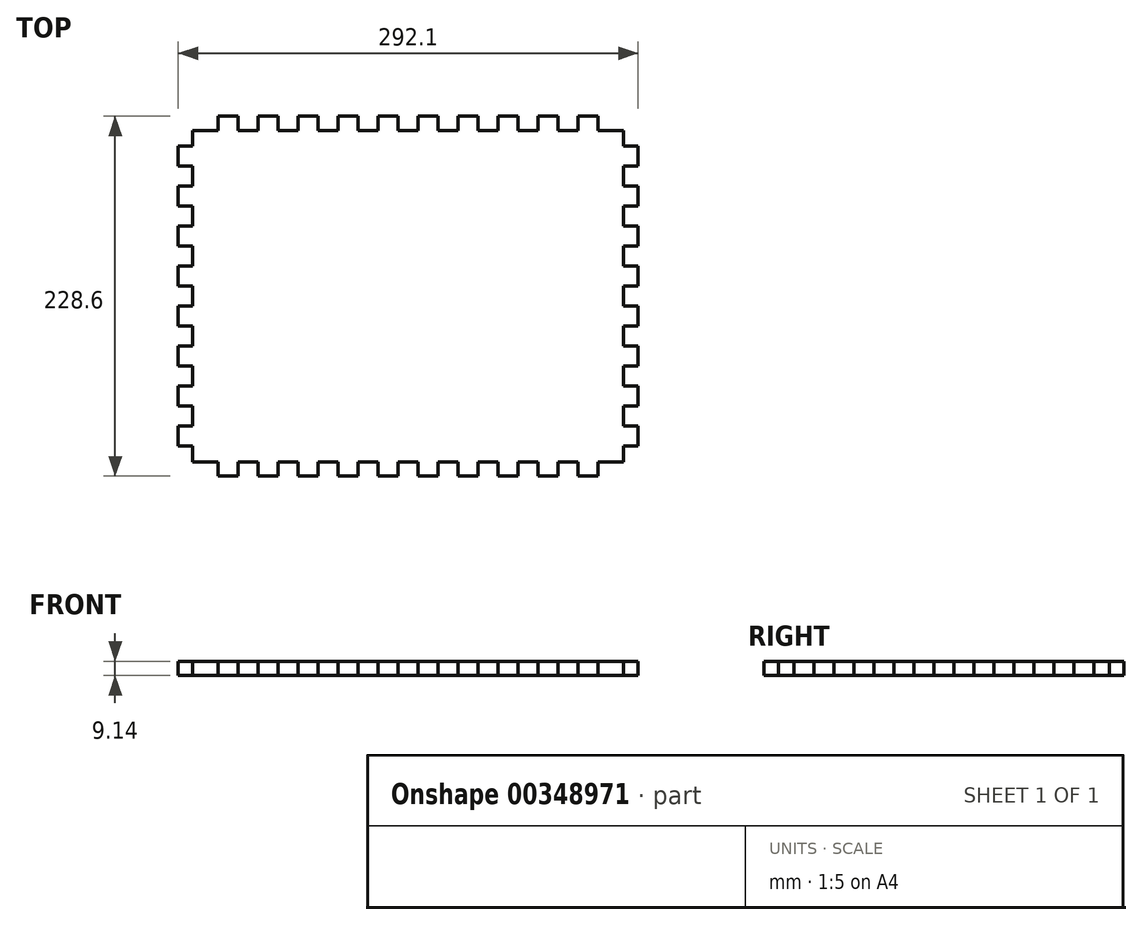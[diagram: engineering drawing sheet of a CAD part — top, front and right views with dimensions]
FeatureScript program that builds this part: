
annotation { "Feature Type Name" : "Feature", "Feature Type Description" : "" }
export const myFeature = defineFeature(function(context is Context, id is Id, definition is map)
    precondition{}
    {
        {
            var Q0;
            Q0=qCreatedBy(makeId("Top.planeOp"),FACE);
            var sketch = newSketch(context, id + "F0", { "sketchPlane" : qUnion([Q0])});
            skLineSegment(sketch, "E0.bottom", {"start": v(0, 0) * mm, "end": v(25.4, 0) * mm, "construction": true});
            skLineSegment(sketch, "E1.bottom", {"start": v(9.14, -9.14) * mm, "end": v(25.4, -9.14) * mm});
            skLineSegment(sketch, "E1.left", {"start": v(9.14, -9.14) * mm, "end": v(9.14, -19.05) * mm});
            skLineSegment(sketch, "E2", {"start": v(9.14, -19.05) * mm, "end": v(0, -19.05) * mm});
            skLineSegment(sketch, "E3", {"start": v(25.4, -9.14) * mm, "end": v(25.4, 0) * mm});
            skLineSegment(sketch, "E4", {"start": v(38.1, 0) * mm, "end": v(38.1, -9.14) * mm});
            skLineSegment(sketch, "E5.0", {"start": v(50.8, 0) * mm, "end": v(50.8, -9.14) * mm});
            skLineSegment(sketch, "E6.0", {"start": v(63.5, 0) * mm, "end": v(63.5, -9.14) * mm});
            skLineSegment(sketch, "E7.0", {"start": v(76.2, 0) * mm, "end": v(76.2, -9.14) * mm});
            skLineSegment(sketch, "E8.0", {"start": v(88.9, 0) * mm, "end": v(88.9, -9.14) * mm});
            skLineSegment(sketch, "E9.0", {"start": v(101.6, 0) * mm, "end": v(101.6, -9.14) * mm});
            skLineSegment(sketch, "E10.0", {"start": v(114.3, 0) * mm, "end": v(114.3, -9.14) * mm});
            skLineSegment(sketch, "E11.0", {"start": v(127, 0) * mm, "end": v(127, -9.14) * mm});
            skLineSegment(sketch, "E12.0", {"start": v(139.7, 0) * mm, "end": v(139.7, -9.14) * mm});
            skLineSegment(sketch, "E13.trimOffspring", {"start": v(50.8, 0) * mm, "end": v(63.5, 0) * mm});
            skLineSegment(sketch, "E14.trimOffspring", {"start": v(63.5, -9.14) * mm, "end": v(76.2, -9.14) * mm});
            skLineSegment(sketch, "E15.trimOffspring", {"start": v(76.2, 0) * mm, "end": v(88.9, 0) * mm});
            skLineSegment(sketch, "E16.trimOffspring", {"start": v(88.9, -9.14) * mm, "end": v(101.6, -9.14) * mm});
            skLineSegment(sketch, "E17.trimOffspring", {"start": v(101.6, 0) * mm, "end": v(114.3, 0) * mm});
            skLineSegment(sketch, "E18.trimOffspring", {"start": v(114.3, -9.14) * mm, "end": v(127, -9.14) * mm});
            skLineSegment(sketch, "E19.trimOffspring", {"start": v(127, 0) * mm, "end": v(139.7, 0) * mm});
            skLineSegment(sketch, "E20.trimOffspring", {"start": v(139.7, -9.14) * mm, "end": v(146.05, -9.14) * mm});
            skLineSegment(sketch, "E21.trimOffspring", {"start": v(38.1, -9.14) * mm, "end": v(50.8, -9.14) * mm});
            skLineSegment(sketch, "E22", {"start": v(0, -31.75) * mm, "end": v(9.14, -31.75) * mm});
            skLineSegment(sketch, "E23", {"start": v(9.14, -31.75) * mm, "end": v(9.14, -44.45) * mm});
            skLineSegment(sketch, "E24", {"start": v(9.14, -44.45) * mm, "end": v(0, -44.45) * mm});
            skLineSegment(sketch, "E25.0", {"start": v(9.14, -57.15) * mm, "end": v(0, -57.15) * mm});
            skLineSegment(sketch, "E26.0", {"start": v(9.14, -69.85) * mm, "end": v(0, -69.85) * mm});
            skLineSegment(sketch, "E27.0", {"start": v(9.14, -82.55) * mm, "end": v(0, -82.55) * mm});
            skLineSegment(sketch, "E28.0", {"start": v(9.14, -95.25) * mm, "end": v(0, -95.25) * mm});
            skLineSegment(sketch, "E29.0", {"start": v(9.14, -107.95) * mm, "end": v(0, -107.95) * mm});
            skLineSegment(sketch, "E30.trimOffspring", {"start": v(0, -44.45) * mm, "end": v(0, -57.15) * mm});
            skLineSegment(sketch, "E31.trimOffspring", {"start": v(9.14, -57.15) * mm, "end": v(9.14, -69.85) * mm});
            skLineSegment(sketch, "E32.trimOffspring", {"start": v(0, -69.85) * mm, "end": v(0, -82.55) * mm});
            skLineSegment(sketch, "E33.trimOffspring", {"start": v(9.14, -82.55) * mm, "end": v(9.14, -95.25) * mm});
            skLineSegment(sketch, "E34.trimOffspring", {"start": v(0, -95.25) * mm, "end": v(0, -107.95) * mm});
            skLineSegment(sketch, "E35.trimOffspring", {"start": v(9.14, -107.95) * mm, "end": v(9.14, -114.3) * mm});
            skLineSegment(sketch, "E36", {"start": v(0, 0) * mm, "end": v(0, -19.05) * mm, "construction": true});
            skLineSegment(sketch, "E37", {"start": v(0, -19.05) * mm, "end": v(0, -31.75) * mm});
            skLineSegment(sketch, "E38", {"start": v(25.4, 0) * mm, "end": v(38.1, 0) * mm});
            skLineSegment(sketch, "E39", {"start": v(146.05, -9.14) * mm, "end": v(146.05, -114.3) * mm, "construction": true});
            skLineSegment(sketch, "E40", {"start": v(9.14, -114.3) * mm, "end": v(146.05, -114.3) * mm, "construction": true});
            skLineSegment(sketch, "E41.MirrorCS", {"start": v(9.14, -120.65) * mm, "end": v(9.14, -114.3) * mm});
            skLineSegment(sketch, "E42.MirrorCS", {"start": v(9.14, -120.65) * mm, "end": v(0, -120.65) * mm});
            skLineSegment(sketch, "E43.MirrorCS", {"start": v(0, -133.35) * mm, "end": v(0, -120.65) * mm});
            skLineSegment(sketch, "E44.MirrorCS", {"start": v(9.14, -133.35) * mm, "end": v(0, -133.35) * mm});
            skLineSegment(sketch, "E45.MirrorCS", {"start": v(9.14, -146.05) * mm, "end": v(9.14, -133.35) * mm});
            skLineSegment(sketch, "E46.MirrorCS", {"start": v(9.14, -146.05) * mm, "end": v(0, -146.05) * mm});
            skLineSegment(sketch, "E47.MirrorCS", {"start": v(0, -158.75) * mm, "end": v(0, -146.05) * mm});
            skLineSegment(sketch, "E48.MirrorCS", {"start": v(9.14, -158.75) * mm, "end": v(0, -158.75) * mm});
            skLineSegment(sketch, "E49.MirrorCS", {"start": v(9.14, -171.45) * mm, "end": v(9.14, -158.75) * mm});
            skLineSegment(sketch, "E50.MirrorCS", {"start": v(9.14, -171.45) * mm, "end": v(0, -171.45) * mm});
            skLineSegment(sketch, "E51.MirrorCS", {"start": v(0, -184.15) * mm, "end": v(0, -171.45) * mm});
            skLineSegment(sketch, "E52.MirrorCS", {"start": v(9.14, -184.15) * mm, "end": v(0, -184.15) * mm});
            skLineSegment(sketch, "E53.MirrorCS", {"start": v(9.14, -196.85) * mm, "end": v(9.14, -184.15) * mm});
            skLineSegment(sketch, "E54.MirrorCS", {"start": v(0, -196.85) * mm, "end": v(9.14, -196.85) * mm});
            skLineSegment(sketch, "E55.MirrorCS", {"start": v(0, -209.55) * mm, "end": v(0, -196.85) * mm});
            skLineSegment(sketch, "E56.MirrorCS", {"start": v(9.14, -209.55) * mm, "end": v(0, -209.55) * mm});
            skLineSegment(sketch, "E57.MirrorCS", {"start": v(9.14, -219.46) * mm, "end": v(9.14, -209.55) * mm});
            skLineSegment(sketch, "E58.MirrorCS", {"start": v(9.14, -219.46) * mm, "end": v(25.4, -219.46) * mm});
            skLineSegment(sketch, "E59.MirrorCS", {"start": v(25.4, -219.46) * mm, "end": v(25.4, -228.6) * mm});
            skLineSegment(sketch, "E60.MirrorCS", {"start": v(25.4, -228.6) * mm, "end": v(38.1, -228.6) * mm});
            skLineSegment(sketch, "E61.MirrorCS", {"start": v(38.1, -228.6) * mm, "end": v(38.1, -219.46) * mm});
            skLineSegment(sketch, "E62.MirrorCS", {"start": v(38.1, -219.46) * mm, "end": v(50.8, -219.46) * mm});
            skLineSegment(sketch, "E63.MirrorCS", {"start": v(50.8, -228.6) * mm, "end": v(50.8, -219.46) * mm});
            skLineSegment(sketch, "E64.MirrorCS", {"start": v(50.8, -228.6) * mm, "end": v(63.5, -228.6) * mm});
            skLineSegment(sketch, "E65.MirrorCS", {"start": v(63.5, -228.6) * mm, "end": v(63.5, -219.46) * mm});
            skLineSegment(sketch, "E66.MirrorCS", {"start": v(63.5, -219.46) * mm, "end": v(76.2, -219.46) * mm});
            skLineSegment(sketch, "E67.MirrorCS", {"start": v(76.2, -228.6) * mm, "end": v(76.2, -219.46) * mm});
            skLineSegment(sketch, "E68.MirrorCS", {"start": v(76.2, -228.6) * mm, "end": v(88.9, -228.6) * mm});
            skLineSegment(sketch, "E69.MirrorCS", {"start": v(88.9, -228.6) * mm, "end": v(88.9, -219.46) * mm});
            skLineSegment(sketch, "E70.MirrorCS", {"start": v(88.9, -219.46) * mm, "end": v(101.6, -219.46) * mm});
            skLineSegment(sketch, "E71.MirrorCS", {"start": v(101.6, -228.6) * mm, "end": v(101.6, -219.46) * mm});
            skLineSegment(sketch, "E72.MirrorCS", {"start": v(101.6, -228.6) * mm, "end": v(114.3, -228.6) * mm});
            skLineSegment(sketch, "E73.MirrorCS", {"start": v(114.3, -219.46) * mm, "end": v(127, -219.46) * mm});
            skLineSegment(sketch, "E74.MirrorCS", {"start": v(127, -228.6) * mm, "end": v(127, -219.46) * mm});
            skLineSegment(sketch, "E75.MirrorCS", {"start": v(127, -228.6) * mm, "end": v(139.7, -228.6) * mm});
            skLineSegment(sketch, "E76.MirrorCS", {"start": v(139.7, -228.6) * mm, "end": v(139.7, -219.46) * mm});
            skLineSegment(sketch, "E77.MirrorCS", {"start": v(139.7, -219.46) * mm, "end": v(146.05, -219.46) * mm});
            skLineSegment(sketch, "E78.MirrorCS", {"start": v(114.3, -228.6) * mm, "end": v(114.3, -219.46) * mm});
            skLineSegment(sketch, "E79.MirrorCS", {"start": v(152.4, -9.14) * mm, "end": v(146.05, -9.14) * mm});
            skLineSegment(sketch, "E80.MirrorCS", {"start": v(152.4, 0) * mm, "end": v(152.4, -9.14) * mm});
            skLineSegment(sketch, "E81.MirrorCS", {"start": v(165.1, 0) * mm, "end": v(152.4, 0) * mm});
            skLineSegment(sketch, "E82.MirrorCS", {"start": v(165.1, 0) * mm, "end": v(165.1, -9.14) * mm});
            skLineSegment(sketch, "E83.MirrorCS", {"start": v(177.8, -9.14) * mm, "end": v(165.1, -9.14) * mm});
            skLineSegment(sketch, "E84.MirrorCS", {"start": v(177.8, 0) * mm, "end": v(177.8, -9.14) * mm});
            skLineSegment(sketch, "E85.MirrorCS", {"start": v(190.5, 0) * mm, "end": v(177.8, 0) * mm});
            skLineSegment(sketch, "E86.MirrorCS", {"start": v(190.5, 0) * mm, "end": v(190.5, -9.14) * mm});
            skLineSegment(sketch, "E87.MirrorCS", {"start": v(203.2, -9.14) * mm, "end": v(190.5, -9.14) * mm});
            skLineSegment(sketch, "E88.MirrorCS", {"start": v(203.2, 0) * mm, "end": v(203.2, -9.14) * mm});
            skLineSegment(sketch, "E89.MirrorCS", {"start": v(215.9, 0) * mm, "end": v(203.2, 0) * mm});
            skLineSegment(sketch, "E90.MirrorCS", {"start": v(215.9, 0) * mm, "end": v(215.9, -9.14) * mm});
            skLineSegment(sketch, "E91.MirrorCS", {"start": v(228.6, -9.14) * mm, "end": v(215.9, -9.14) * mm});
            skLineSegment(sketch, "E92.MirrorCS", {"start": v(228.6, 0) * mm, "end": v(228.6, -9.14) * mm});
            skLineSegment(sketch, "E93.MirrorCS", {"start": v(241.3, 0) * mm, "end": v(228.6, 0) * mm});
            skLineSegment(sketch, "E94.MirrorCS", {"start": v(241.3, 0) * mm, "end": v(241.3, -9.14) * mm});
            skLineSegment(sketch, "E95.MirrorCS", {"start": v(254, -9.14) * mm, "end": v(241.3, -9.14) * mm});
            skLineSegment(sketch, "E96.MirrorCS", {"start": v(254, 0) * mm, "end": v(254, -9.14) * mm});
            skLineSegment(sketch, "E97.MirrorCS", {"start": v(266.7, 0) * mm, "end": v(254, 0) * mm});
            skLineSegment(sketch, "E98.MirrorCS", {"start": v(266.7, -9.14) * mm, "end": v(266.7, 0) * mm});
            skLineSegment(sketch, "E99.MirrorCS", {"start": v(282.96, -9.14) * mm, "end": v(266.7, -9.14) * mm});
            skLineSegment(sketch, "E100.MirrorCS", {"start": v(282.96, -31.75) * mm, "end": v(282.96, -44.45) * mm});
            skLineSegment(sketch, "E101.MirrorCS", {"start": v(282.96, -107.95) * mm, "end": v(282.96, -114.3) * mm});
            skLineSegment(sketch, "E102.MirrorCS", {"start": v(282.96, -120.65) * mm, "end": v(282.96, -114.3) * mm});
            skLineSegment(sketch, "E103.MirrorCS", {"start": v(292.1, -95.25) * mm, "end": v(292.1, -107.95) * mm});
            skLineSegment(sketch, "E104.MirrorCS", {"start": v(282.96, -171.45) * mm, "end": v(282.96, -158.75) * mm});
            skLineSegment(sketch, "E105.MirrorCS", {"start": v(282.96, -209.55) * mm, "end": v(292.1, -209.55) * mm});
            skLineSegment(sketch, "E106.MirrorCS", {"start": v(282.96, -57.15) * mm, "end": v(292.1, -57.15) * mm});
            skLineSegment(sketch, "E107.MirrorCS", {"start": v(282.96, -196.85) * mm, "end": v(282.96, -184.15) * mm});
            skLineSegment(sketch, "E108.MirrorCS", {"start": v(292.1, -31.75) * mm, "end": v(282.96, -31.75) * mm});
            skLineSegment(sketch, "E109.MirrorCS", {"start": v(292.1, -44.45) * mm, "end": v(292.1, -57.15) * mm});
            skLineSegment(sketch, "E110.MirrorCS", {"start": v(282.96, -82.55) * mm, "end": v(292.1, -82.55) * mm});
            skLineSegment(sketch, "E111.MirrorCS", {"start": v(282.96, -44.45) * mm, "end": v(292.1, -44.45) * mm});
            skLineSegment(sketch, "E112.MirrorCS", {"start": v(292.1, -133.35) * mm, "end": v(292.1, -120.65) * mm});
            skLineSegment(sketch, "E113.MirrorCS", {"start": v(282.96, -146.05) * mm, "end": v(282.96, -133.35) * mm});
            skLineSegment(sketch, "E114.MirrorCS", {"start": v(282.96, -19.05) * mm, "end": v(292.1, -19.05) * mm});
            skLineSegment(sketch, "E115.MirrorCS", {"start": v(282.96, -95.25) * mm, "end": v(292.1, -95.25) * mm});
            skLineSegment(sketch, "E116.MirrorCS", {"start": v(292.1, -196.85) * mm, "end": v(282.96, -196.85) * mm});
            skLineSegment(sketch, "E117.MirrorCS", {"start": v(292.1, -158.75) * mm, "end": v(292.1, -146.05) * mm});
            skLineSegment(sketch, "E118.MirrorCS", {"start": v(282.96, -107.95) * mm, "end": v(292.1, -107.95) * mm});
            skLineSegment(sketch, "E119.MirrorCS", {"start": v(282.96, -69.85) * mm, "end": v(292.1, -69.85) * mm});
            skLineSegment(sketch, "E120.MirrorCS", {"start": v(292.1, -184.15) * mm, "end": v(292.1, -171.45) * mm});
            skLineSegment(sketch, "E121.MirrorCS", {"start": v(282.96, -184.15) * mm, "end": v(292.1, -184.15) * mm});
            skLineSegment(sketch, "E122.MirrorCS", {"start": v(292.1, -69.85) * mm, "end": v(292.1, -82.55) * mm});
            skLineSegment(sketch, "E123.MirrorCS", {"start": v(282.96, -158.75) * mm, "end": v(292.1, -158.75) * mm});
            skLineSegment(sketch, "E124.MirrorCS", {"start": v(282.96, -120.65) * mm, "end": v(292.1, -120.65) * mm});
            skLineSegment(sketch, "E125.MirrorCS", {"start": v(282.96, -146.05) * mm, "end": v(292.1, -146.05) * mm});
            skLineSegment(sketch, "E126.MirrorCS", {"start": v(292.1, -19.05) * mm, "end": v(292.1, -31.75) * mm});
            skLineSegment(sketch, "E127.MirrorCS", {"start": v(282.96, -171.45) * mm, "end": v(292.1, -171.45) * mm});
            skLineSegment(sketch, "E128.MirrorCS", {"start": v(282.96, -82.55) * mm, "end": v(282.96, -95.25) * mm});
            skLineSegment(sketch, "E129.MirrorCS", {"start": v(292.1, -209.55) * mm, "end": v(292.1, -196.85) * mm});
            skLineSegment(sketch, "E130.MirrorCS", {"start": v(282.96, -133.35) * mm, "end": v(292.1, -133.35) * mm});
            skLineSegment(sketch, "E131.MirrorCS", {"start": v(282.96, -57.15) * mm, "end": v(282.96, -69.85) * mm});
            skLineSegment(sketch, "E132", {"start": v(282.96, -9.14) * mm, "end": v(282.96, -19.05) * mm});
            skLineSegment(sketch, "E133.MirrorCS", {"start": v(254, -228.6) * mm, "end": v(254, -219.46) * mm});
            skLineSegment(sketch, "E134.MirrorCS", {"start": v(190.5, -228.6) * mm, "end": v(190.5, -219.46) * mm});
            skLineSegment(sketch, "E135.MirrorCS", {"start": v(241.3, -228.6) * mm, "end": v(241.3, -219.46) * mm});
            skLineSegment(sketch, "E136.MirrorCS", {"start": v(177.8, -228.6) * mm, "end": v(177.8, -219.46) * mm});
            skLineSegment(sketch, "E137.MirrorCS", {"start": v(215.9, -228.6) * mm, "end": v(203.2, -228.6) * mm});
            skLineSegment(sketch, "E138.MirrorCS", {"start": v(190.5, -228.6) * mm, "end": v(177.8, -228.6) * mm});
            skLineSegment(sketch, "E139.MirrorCS", {"start": v(203.2, -228.6) * mm, "end": v(203.2, -219.46) * mm});
            skLineSegment(sketch, "E140.MirrorCS", {"start": v(228.6, -228.6) * mm, "end": v(228.6, -219.46) * mm});
            skLineSegment(sketch, "E141.MirrorCS", {"start": v(165.1, -228.6) * mm, "end": v(165.1, -219.46) * mm});
            skLineSegment(sketch, "E142.MirrorCS", {"start": v(266.7, -219.46) * mm, "end": v(266.7, -228.6) * mm});
            skLineSegment(sketch, "E143.MirrorCS", {"start": v(215.9, -228.6) * mm, "end": v(215.9, -219.46) * mm});
            skLineSegment(sketch, "E144.MirrorCS", {"start": v(266.7, -228.6) * mm, "end": v(254, -228.6) * mm});
            skLineSegment(sketch, "E145.MirrorCS", {"start": v(241.3, -228.6) * mm, "end": v(228.6, -228.6) * mm});
            skLineSegment(sketch, "E146.MirrorCS", {"start": v(228.6, -219.46) * mm, "end": v(215.9, -219.46) * mm});
            skLineSegment(sketch, "E147.MirrorCS", {"start": v(254, -219.46) * mm, "end": v(241.3, -219.46) * mm});
            skLineSegment(sketch, "E148.MirrorCS", {"start": v(177.8, -219.46) * mm, "end": v(165.1, -219.46) * mm});
            skLineSegment(sketch, "E149.MirrorCS", {"start": v(203.2, -219.46) * mm, "end": v(190.5, -219.46) * mm});
            skLineSegment(sketch, "E150.MirrorCS", {"start": v(282.96, -219.46) * mm, "end": v(266.7, -219.46) * mm});
            skLineSegment(sketch, "E151.MirrorCS", {"start": v(282.96, -219.46) * mm, "end": v(282.96, -209.55) * mm});
            skLineSegment(sketch, "E152.MirrorCS", {"start": v(152.4, -228.6) * mm, "end": v(152.4, -219.46) * mm});
            skLineSegment(sketch, "E153.MirrorCS", {"start": v(152.4, -219.46) * mm, "end": v(146.05, -219.46) * mm});
            skLineSegment(sketch, "E154", {"start": v(152.4, -228.6) * mm, "end": v(165.1, -228.6) * mm});
            skSolve(sketch);
        }
        {
            var Q0;
            Q0=makeQuery(id+"F0.imprint","IMPRINT",FACE,{"disambiguationData":[TD([[makeQuery(id+"F0.imprint","IMPRINT",EDGE,{"derivedFrom":sQuery(id+"F0.wireOp",EDGE,"E1.bottom")}),-1.0]])]});
            extrude(context, id + "F1", {"entities" : qUnion([Q0]), "depth" : 9.14 * mm});
        }
    });
